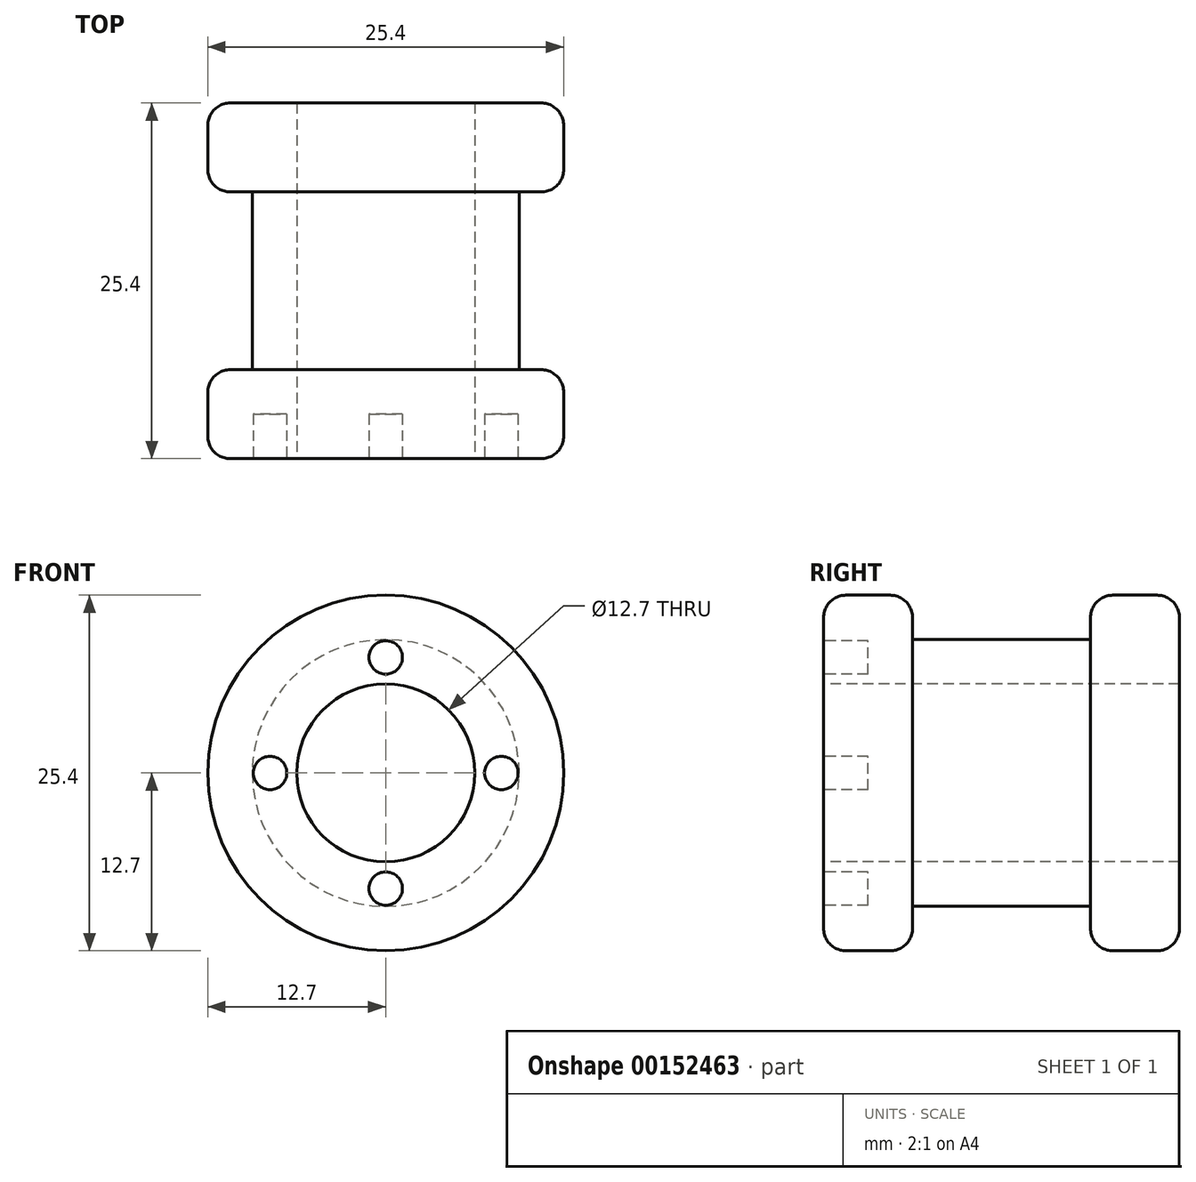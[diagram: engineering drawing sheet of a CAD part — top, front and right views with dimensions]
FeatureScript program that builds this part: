
annotation { "Feature Type Name" : "Feature", "Feature Type Description" : "" }
export const myFeature = defineFeature(function(context is Context, id is Id, definition is map)
    precondition{}
    {
        {
            var Q0;
            Q0=qCreatedBy(makeId("Front.planeOp"),FACE);
            var sketch = newSketch(context, id + "F0", { "sketchPlane" : qUnion([Q0])});
            skCircle(sketch, "E0", {"center": v(0, 0) * mm, "radius": 12.7 * mm});
            skSolve(sketch);
        }
        {
            var Q0;
            Q0 = qSketchRegion(id + "F0", true);
            extrude(context, id + "F1", {"entities" : qUnion([Q0]), "depth" : 6.35 * mm});
        }
        {
            var Q0;
            Q0=makeQuery(id+"F1.opExtrude","CAP_FACE",FACE,{"disambiguationData":[OSD([sQuery(id+"F0.wireOp",EDGE,"E0")])],"isStart":false});
            var sketch = newSketch(context, id + "F2", { "sketchPlane" : qUnion([Q0])});
            skCircle(sketch, "E1", {"center": v(0, 0) * mm, "radius": 9.53 * mm});
            skSolve(sketch);
        }
        {
            var Q0;
            Q0 = qSketchRegion(id + "F2", true);
            extrude(context, id + "F3", {"entities" : qUnion([Q0]), "operationType" : NewBodyOperationType.ADD, "depth" : 12.7 * mm});
        }
        {
            var Q0;
            Q0=makeQuery(id+"F3.opExtrude","CAP_FACE",FACE,{"disambiguationData":[OSD([sQuery(id+"F2.wireOp",EDGE,"E1")])],"isStart":false});
            var sketch = newSketch(context, id + "F4", { "sketchPlane" : qUnion([Q0])});
            skCircle(sketch, "E2", {"center": v(0, 0) * mm, "radius": 12.7 * mm});
            skSolve(sketch);
        }
        {
            var Q0;
            Q0 = qSketchRegion(id + "F4", true);
            extrude(context, id + "F5", {"entities" : qUnion([Q0]), "operationType" : NewBodyOperationType.ADD, "depth" : 6.35 * mm});
        }
        {
            var Q0;
            Q0=makeQuery(id+"F5.opExtrude","CAP_EDGE",EDGE,{"disambiguationData":[OSD([sQuery(id+"F4.wireOp",EDGE,"E2")])],"isStart":false});
            var Q1;
            Q1=makeQuery(id+"F5.opExtrude","CAP_EDGE",EDGE,{"disambiguationData":[OSD([sQuery(id+"F4.wireOp",EDGE,"E2")])],"isStart":true});
            var Q2;
            Q2=makeQuery(id+"F1.opExtrude","CAP_EDGE",EDGE,{"disambiguationData":[OSD([sQuery(id+"F0.wireOp",EDGE,"E0")])],"isStart":false});
            var Q3;
            Q3=makeQuery(id+"F1.opExtrude","CAP_EDGE",EDGE,{"disambiguationData":[OSD([sQuery(id+"F0.wireOp",EDGE,"E0")])],"isStart":true});
            fillet(context, id + "F6", {"entities" : qUnion([Q0, Q1, Q2, Q3]), "radius" : 1.6 * mm, "tangentPropagation" : true, "allowEdgeOverflow" : false});
        }
        {
            var Q0;
            Q0=makeQuery(id+"F5.opExtrude","CAP_FACE",FACE,{"disambiguationData":[OSD([sQuery(id+"F4.wireOp",EDGE,"E2")])],"isStart":false});
            var sketch = newSketch(context, id + "F7", { "sketchPlane" : qUnion([Q0])});
            skCircle(sketch, "E3", {"center": v(-8.26, 0) * mm, "radius": 1.2 * mm});
            skCircle(sketch, "E4.1.0", {"center": v(0, -8.26) * mm, "radius": 1.2 * mm});
            skCircle(sketch, "E4.2.0", {"center": v(8.26, 0) * mm, "radius": 1.2 * mm});
            skCircle(sketch, "E4.3.0", {"center": v(0, 8.26) * mm, "radius": 1.2 * mm});
            skPoint(sketch, "E4.center", {"position": v(0, 0) * mm});
            skSolve(sketch);
        }
        {
            var Q0;
            Q0 = qSketchRegion(id + "F7", true);
            extrude(context, id + "F8", {"entities" : qUnion([Q0]), "operationType" : NewBodyOperationType.REMOVE, "oppositeDirection" : true, "depth" : 3.17 * mm});
        }
        {
            var Q0;
            Q0=makeQuery(id+"F5.opExtrude","CAP_FACE",FACE,{"disambiguationData":[OSD([sQuery(id+"F4.wireOp",EDGE,"E2")])],"isStart":false});
            var sketch = newSketch(context, id + "F9", { "sketchPlane" : qUnion([Q0])});
            skCircle(sketch, "E5", {"center": v(0, 0) * mm, "radius": 6.35 * mm});
            skSolve(sketch);
        }
        {
            var Q0;
            Q0 = qSketchRegion(id + "F9", true);
            extrude(context, id + "F10", {"entities" : qUnion([Q0]), "operationType" : NewBodyOperationType.REMOVE, "endBound" : BoundingType.THROUGH_ALL, "oppositeDirection" : true, "depth" : 25.4 * mm});
        }
    });
